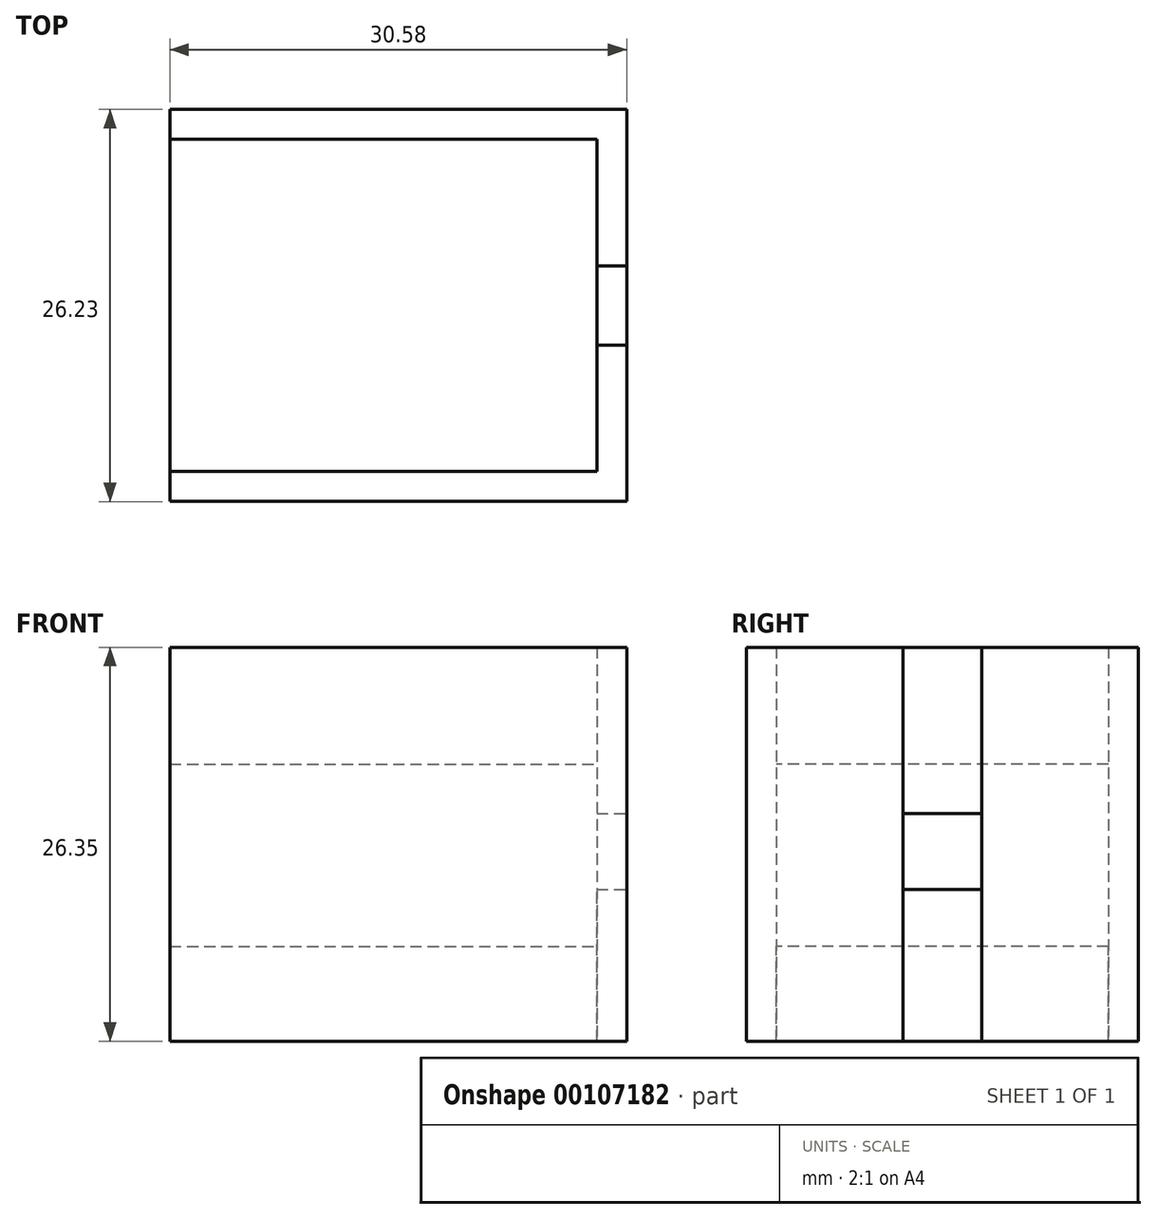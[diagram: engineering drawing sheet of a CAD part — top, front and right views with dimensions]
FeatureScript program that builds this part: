
annotation { "Feature Type Name" : "Feature", "Feature Type Description" : "" }
export const myFeature = defineFeature(function(context is Context, id is Id, definition is map)
    precondition{}
    {
        {
            var Q0;
            Q0=qCreatedBy(makeId("Top.planeOp"),FACE);
            var sketch = newSketch(context, id + "F0", { "sketchPlane" : qUnion([Q0])});
            skLineSegment(sketch, "E0.bottom", {"start": v(-20.64, 14.7) * mm, "end": v(9.94, 14.7) * mm});
            skLineSegment(sketch, "E0.top", {"start": v(-20.64, -11.52) * mm, "end": v(9.94, -11.52) * mm});
            skLineSegment(sketch, "E0.left", {"start": v(-20.64, 14.7) * mm, "end": v(-20.64, -11.52) * mm});
            skLineSegment(sketch, "E0.right", {"start": v(9.94, 14.7) * mm, "end": v(9.94, -11.52) * mm});
            skPoint(sketch, "E1", {"position": v(-20.64, 12.7) * mm});
            skPoint(sketch, "E2", {"position": v(-20.64, -9.53) * mm});
            skPoint(sketch, "E3", {"position": v(7.94, 14.7) * mm});
            skLineSegment(sketch, "E4", {"start": v(-20.64, 12.7) * mm, "end": v(7.94, 12.7) * mm});
            skLineSegment(sketch, "E5", {"start": v(7.94, 12.7) * mm, "end": v(7.94, 4.23) * mm});
            skLineSegment(sketch, "E6", {"start": v(7.94, -9.52) * mm, "end": v(-20.64, -9.53) * mm});
            skPoint(sketch, "E7", {"position": v(7.94, 4.23) * mm});
            skPoint(sketch, "E8", {"position": v(7.94, -1.06) * mm});
            skLineSegment(sketch, "E9", {"start": v(7.94, 4.23) * mm, "end": v(9.94, 4.23) * mm});
            skLineSegment(sketch, "E10", {"start": v(7.94, -1.06) * mm, "end": v(9.94, -1.06) * mm});
            skLineSegment(sketch, "E11.trimOffspring", {"start": v(7.94, -1.06) * mm, "end": v(7.94, -9.52) * mm});
            skLineSegment(sketch, "E12", {"start": v(7.94, 4.23) * mm, "end": v(7.94, -1.06) * mm});
            skSolve(sketch);
        }
        {
            var Q0;
            {var subQ1=sQuery(id+"F0.wireOp",EDGE,"E4");Q0=makeQuery(id+"F0.imprint","IMPRINT",FACE,{"disambiguationData":[TD([[makeQuery(id+"F0.imprint","IMPRINT",EDGE,{"derivedFrom":subQ1}),-1.0]])]});}
            extrude(context, id + "F1", {"entities" : qUnion([Q0]), "depth" : 20 * mm, "hasSecondDirection" : true, "secondDirectionOppositeDirection" : false, "secondDirectionDepth" : 12.2 * mm});
        }
        {
            var Q0;
            {var subQ1=sQuery(id+"F0.wireOp",EDGE,"E4");Q0=makeQuery(id+"F0.imprint","IMPRINT",FACE,{"disambiguationData":[TD([[makeQuery(id+"F0.imprint","IMPRINT",EDGE,{"derivedFrom":subQ1}),-1.0]])]});}
            extrude(context, id + "F2", {"entities" : qUnion([Q0]), "oppositeDirection" : true, "depth" : 6.35 * mm});
        }
        {
            var Q0;
            {var subQ2=sQuery(id+"F0.wireOp",EDGE,"E0.bottom");Q0=makeQuery(id+"F0.imprint","IMPRINT",FACE,{"disambiguationData":[TD([[makeQuery(id+"F0.imprint","IMPRINT",EDGE,{"derivedFrom":subQ2}),-1.0]])]});}
            var Q1;
            {var subQ2=sQuery(id+"F0.wireOp",EDGE,"E0.top");Q1=makeQuery(id+"F0.imprint","IMPRINT",FACE,{"disambiguationData":[TD([[makeQuery(id+"F0.imprint","IMPRINT",EDGE,{"derivedFrom":subQ2}),1.0]])]});}
            extrude(context, id + "F3", {"entities" : qUnion([Q0, Q1]), "depth" : 20 * mm, "hasSecondDirection" : true, "secondDirectionOppositeDirection" : true, "secondDirectionDepth" : 6.35 * mm});
        }
        {
            var Q0;
            {var subQ0=sQuery(id+"F0.wireOp",EDGE,"E9");Q0=makeQuery(id+"F0.imprint","IMPRINT",FACE,{"disambiguationData":[TD([[makeQuery(id+"F0.imprint","IMPRINT",EDGE,{"derivedFrom":subQ0}),-1.0]])]});}
            extrude(context, id + "F4", {"entities" : qUnion([Q0]), "oppositeDirection" : true, "depth" : 6.35 * mm, "hasSecondDirection" : true, "secondDirectionOppositeDirection" : false, "secondDirectionDepth" : 3.8 * mm});
        }
        {
            var Q0;
            {var subQ0=sQuery(id+"F0.wireOp",EDGE,"E9");Q0=makeQuery(id+"F0.imprint","IMPRINT",FACE,{"disambiguationData":[TD([[makeQuery(id+"F0.imprint","IMPRINT",EDGE,{"derivedFrom":subQ0}),-1.0]])]});}
            extrude(context, id + "F5", {"entities" : qUnion([Q0]), "depth" : 20 * mm, "hasSecondDirection" : true, "secondDirectionOppositeDirection" : false, "secondDirectionDepth" : 8.9 * mm});
        }
    });
